# Revit family: QF_COMENDA_TL48BT
name_source: partatom
category: Attrezzature speciali
units: mm (PartAtom-declared; Revit-internal decimal feet)

## family parameters
Basato su piano di lavoro = No
Condiviso = No
Numero OmniClass = 23.40.40.14
Punto di calcolo locali = No
Quota connettore circolare = Usa diametro
Sempre verticale = Sì
Taglio con vuoti quando caricato = No
Tipo di parte = Normale
Titolo OmniClass = Food Service Equipment

## types (1)
- H57206
    Altezza = 705 mm  [stored 2.31299 ft]
    Altezza allacciamento elettrico da pavimento finito = 55 mm  [stored 0.180446 ft]
    Altezza da terra raccordo acqua calda = 55 mm  [stored 0.180446 ft]
    Altezza dello scarico diretto acqua da pavimento finito = 55 mm  [stored 0.180446 ft]
    Corrente di funzionamento normale = 9 A
    Descrizione = MULTIPOWER DOUBLE WALL GLASS WASHER WITH HR DRAIN PUMP AND PERISTALTIC DOSING UNITS AND BREAK TANK
    Diametro dello scarico diretto di acqua = 1 1/2"
    Diametro raccordo acqua calda = 1"
    Fase = 3
    Frequenza = 50 Hz
    Lunghezza = 480 mm  [stored 1.5748 ft]
    Modello = TL48BT
    Numero dei poli = 3
    Peso netto = 49.00 kg
    Potenza elettrica = 5260 W
    Pressione minima acqua calda = 2000.0 Pa
    Produttore = HOONVED
    Profondità = 530 mm  [stored 1.73885 ft]
    Protezione contro le sovracorrenti = 16 A
    Temperatura raccomandata per acqua calda = 50 °C
    Tensione = 400 V
    URL = https://www.hoonved.com
    URL catalogo = https://www.hoonved.com

note: [stored X ft] marks values corroborated as IEEE doubles in the binary element streams (Revit-internal decimal feet)

## geometry (parser evidence)
native form markers: Sweep x5
no freeform markers — native parametric forms only
